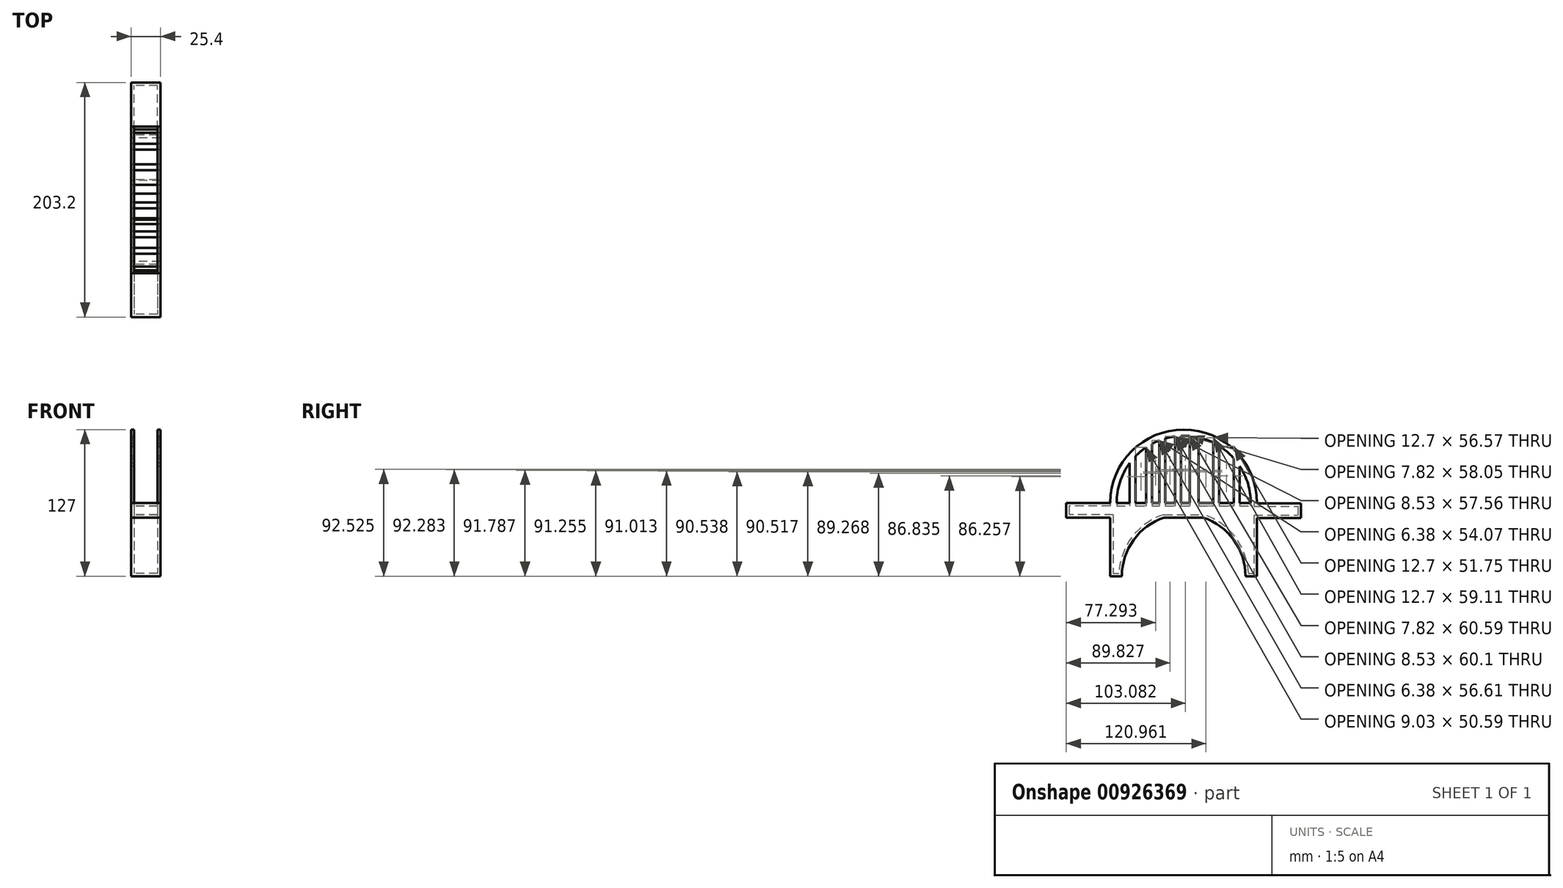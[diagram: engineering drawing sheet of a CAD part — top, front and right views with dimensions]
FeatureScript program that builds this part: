
annotation { "Feature Type Name" : "Feature", "Feature Type Description" : "" }
export const myFeature = defineFeature(function(context is Context, id is Id, definition is map)
    precondition{}
    {
        {
            var Q0;
            Q0=qCreatedBy(makeId("Right.planeOp"),FACE);
            var sketch = newSketch(context, id + "F0", { "sketchPlane" : qUnion([Q0])});
            skLineSegment(sketch, "E0.bottom", {"start": v(-51.78, 37.28) * mm, "end": v(75.22, 37.28) * mm});
            skLineSegment(sketch, "E0.top", {"start": v(-51.78, 24.58) * mm, "end": v(75.22, 24.58) * mm});
            skLineSegment(sketch, "E0.left", {"start": v(-51.78, 37.28) * mm, "end": v(-51.78, 24.58) * mm});
            skLineSegment(sketch, "E0.right", {"start": v(75.22, 37.28) * mm, "end": v(75.22, 24.58) * mm});
            skLineSegment(sketch, "E1.top", {"start": v(-51.78, -26.22) * mm, "end": v(75.22, -26.22) * mm});
            skLineSegment(sketch, "E1.left", {"start": v(-51.78, 24.58) * mm, "end": v(-51.78, -26.22) * mm});
            skLineSegment(sketch, "E1.right", {"start": v(75.22, 24.58) * mm, "end": v(75.22, -26.22) * mm});
            skArc(sketch, "E2", {"start": v(-41.8, -26.22) * mm, "mid": v(11.72, 27.3) * mm, "end": v(65.23, -26.22) * mm});
            skLineSegment(sketch, "E3.bottom", {"start": v(75.22, 36.8) * mm, "end": v(113.32, 36.8) * mm});
            skLineSegment(sketch, "E3.top", {"start": v(75.22, 24.1) * mm, "end": v(113.32, 24.1) * mm});
            skLineSegment(sketch, "E3.left", {"start": v(75.22, 36.8) * mm, "end": v(75.22, 24.1) * mm});
            skLineSegment(sketch, "E3.right", {"start": v(113.32, 36.8) * mm, "end": v(113.32, 24.1) * mm});
            skLineSegment(sketch, "E4.bottom", {"start": v(-51.78, 37.28) * mm, "end": v(-89.88, 37.28) * mm});
            skLineSegment(sketch, "E4.top", {"start": v(-51.78, 24.58) * mm, "end": v(-89.88, 24.58) * mm});
            skLineSegment(sketch, "E4.right", {"start": v(-89.88, 37.28) * mm, "end": v(-89.88, 24.58) * mm});
            skArc(sketch, "E5", {"start": v(75.22, 37.28) * mm, "mid": v(11.72, 100.78) * mm, "end": v(-51.78, 37.28) * mm});
            skArc(sketch, "E6", {"start": v(69.76, 37.28) * mm, "mid": v(11.72, 95.33) * mm, "end": v(-46.33, 37.28) * mm});
            skLineSegment(sketch, "E7", {"start": v(-34.97, 71.79) * mm, "end": v(-34.97, 37.28) * mm});
            skLineSegment(sketch, "E8", {"start": v(-29.89, 77.77) * mm, "end": v(-29.89, 37.28) * mm});
            skLineSegment(sketch, "E9", {"start": v(-20.85, 85.33) * mm, "end": v(-20.85, 37.28) * mm});
            skLineSegment(sketch, "E10", {"start": v(-15.77, 88.4) * mm, "end": v(-15.77, 37.28) * mm});
            skLineSegment(sketch, "E11", {"start": v(-9.4, 91.35) * mm, "end": v(-9.4, 37.28) * mm});
            skLineSegment(sketch, "E12", {"start": v(-4.32, 93.07) * mm, "end": v(-4.32, 37.28) * mm});
            skLineSegment(sketch, "E13", {"start": v(17.11, 95.08) * mm, "end": v(17.11, 37.28) * mm});
            skLineSegment(sketch, "E14", {"start": v(24.73, 93.85) * mm, "end": v(24.73, 37.28) * mm});
            skLineSegment(sketch, "E15", {"start": v(37.43, 89.32) * mm, "end": v(37.43, 37.28) * mm});
            skLineSegment(sketch, "E16", {"start": v(42.51, 86.49) * mm, "end": v(42.51, 37.28) * mm});
            skLineSegment(sketch, "E17", {"start": v(55.21, 75.72) * mm, "end": v(55.21, 37.28) * mm});
            skLineSegment(sketch, "E18", {"start": v(60.3, 69.06) * mm, "end": v(60.3, 37.28) * mm});
            skLineSegment(sketch, "E19", {"start": v(4.21, 94.84) * mm, "end": v(4.21, 37.28) * mm});
            skLineSegment(sketch, "E20", {"start": v(9.3, 95.28) * mm, "end": v(9.3, 37.28) * mm});
            skPoint(sketch, "E21.startSnap0", {"position": v(55.21, 56.5) * mm});
            skSolve(sketch);
        }
        {
            var Q0;
            {var subQ0=sQuery(id+"F0.wireOp",EDGE,"E1.left");Q0=makeQuery(id+"F0.imprint","IMPRINT",FACE,{"disambiguationData":[TD([[makeQuery(id+"F0.imprint","IMPRINT",EDGE,{"derivedFrom":subQ0}),1.0]])]});}
            var Q1;
            {var subQ2=sQuery(id+"F0.wireOp",EDGE,"E1.top");var subQ4=sQuery(id+"F0.wireOp",EDGE,"E2");var subQ5=makeQuery(id+"F0.imprint","INTERSECT",VERTEX,{"disambiguationData":[OD(1.0)],"derivedFrom":[subQ2,subQ4]});Q1=makeQuery(id+"F0.imprint","IMPRINT",FACE,{"disambiguationData":[TD([[makeQuery(id+"F0.imprint","IMPRINT",EDGE,{"disambiguationData":[TD([[subQ5,-1.0]])],"derivedFrom":subQ2}),1.0]])]});}
            var Q2;
            {var subQ7=sQuery(id+"F0.wireOp",EDGE,"E0.left");Q2=makeQuery(id+"F0.imprint","IMPRINT",FACE,{"disambiguationData":[TD([[makeQuery(id+"F0.imprint","IMPRINT",EDGE,{"derivedFrom":subQ7}),1.0]])]});}
            var Q3;
            Q3=makeQuery(id+"F0.imprint","IMPRINT",FACE,{"disambiguationData":[TD([[makeQuery(id+"F0.imprint","IMPRINT",EDGE,{"derivedFrom":sQuery(id+"F0.wireOp",EDGE,"E0.left")}),-1.0]])]});
            var Q4;
            {var subQ0=sQuery(id+"F0.wireOp",EDGE,"E3.bottom");Q4=makeQuery(id+"F0.imprint","IMPRINT",FACE,{"disambiguationData":[TD([[makeQuery(id+"F0.imprint","IMPRINT",EDGE,{"derivedFrom":subQ0}),-1.0]])]});}
            var Q5;
            {var subQ0=sQuery(id+"F0.wireOp",EDGE,"E2");var subQ1=sQuery(id+"F0.wireOp",EDGE,"E0.top");var subQ2=makeQuery(id+"F0.imprint","INTERSECT",VERTEX,{"disambiguationData":[OD(0.0)],"derivedFrom":[subQ1,subQ0]});Q5=makeQuery(id+"F0.imprint","IMPRINT",FACE,{"disambiguationData":[TD([[makeQuery(id+"F0.imprint","IMPRINT",EDGE,{"disambiguationData":[TD([[subQ2,1.0]])],"derivedFrom":subQ1}),1.0]])]});}
            var Q6;
            {var subQ8=sQuery(id+"F0.wireOp",EDGE,"E5");Q6=makeQuery(id+"F0.imprint","IMPRINT",FACE,{"disambiguationData":[TD([[makeQuery(id+"F0.imprint","IMPRINT",EDGE,{"derivedFrom":subQ8}),1.0]])]});}
            var Q7;
            {var subQ0=sQuery(id+"F0.wireOp",EDGE,"E7");Q7=makeQuery(id+"F0.imprint","IMPRINT",FACE,{"disambiguationData":[TD([[makeQuery(id+"F0.imprint","IMPRINT",EDGE,{"derivedFrom":subQ0}),1.0]])]});}
            var Q8;
            {var subQ0=sQuery(id+"F0.wireOp",EDGE,"E9");Q8=makeQuery(id+"F0.imprint","IMPRINT",FACE,{"disambiguationData":[TD([[makeQuery(id+"F0.imprint","IMPRINT",EDGE,{"derivedFrom":subQ0}),1.0]])]});}
            var Q9;
            {var subQ0=sQuery(id+"F0.wireOp",EDGE,"E11");Q9=makeQuery(id+"F0.imprint","IMPRINT",FACE,{"disambiguationData":[TD([[makeQuery(id+"F0.imprint","IMPRINT",EDGE,{"derivedFrom":subQ0}),1.0]])]});}
            var Q10;
            {var subQ2=sQuery(id+"F0.wireOp",EDGE,"E19");Q10=makeQuery(id+"F0.imprint","IMPRINT",FACE,{"disambiguationData":[TD([[makeQuery(id+"F0.imprint","IMPRINT",EDGE,{"derivedFrom":subQ2}),1.0]])]});}
            var Q11;
            {var subQ0=sQuery(id+"F0.wireOp",EDGE,"E13");Q11=makeQuery(id+"F0.imprint","IMPRINT",FACE,{"disambiguationData":[TD([[makeQuery(id+"F0.imprint","IMPRINT",EDGE,{"derivedFrom":subQ0}),1.0]])]});}
            var Q12;
            {var subQ2=sQuery(id+"F0.wireOp",EDGE,"E15");Q12=makeQuery(id+"F0.imprint","IMPRINT",FACE,{"disambiguationData":[TD([[makeQuery(id+"F0.imprint","IMPRINT",EDGE,{"derivedFrom":subQ2}),1.0]])]});}
            var Q13;
            {var subQ0=sQuery(id+"F0.wireOp",EDGE,"E17");Q13=makeQuery(id+"F0.imprint","IMPRINT",FACE,{"disambiguationData":[TD([[makeQuery(id+"F0.imprint","IMPRINT",EDGE,{"derivedFrom":subQ0}),1.0]])]});}
            extrude(context, id + "F1", {"entities" : qUnion([Q0, Q1, Q2, Q3, Q4, Q5, Q6, Q7, Q8, Q9, Q10, Q11, Q12, Q13]), "depth" : 25.4 * mm, "offsetDistance" : 25.4 * mm});
        }
        {
            var Q0;
            {var subQ0=sQuery(id+"F0.wireOp",EDGE,"E6");Q0=makeQuery(id+"F1.opExtrude","SWEPT_FACE",FACE,{"disambiguationData":[OSD([subQ0]),TDD([makeQuery(id+"F0.imprint","IMPRINT",EDGE,{"disambiguationData":[TD([[makeQuery(id+"F0.imprint","INTERSECT",VERTEX,{"derivedFrom":[subQ0,sQuery(id+"F0.wireOp",EDGE,"E10")]}),1.0]])],"derivedFrom":subQ0})])]});}
            var Q1;
            {var subQ0=sQuery(id+"F0.wireOp",EDGE,"E6");Q1=makeQuery(id+"F1.opExtrude","SWEPT_FACE",FACE,{"disambiguationData":[OSD([subQ0]),TDD([makeQuery(id+"F0.imprint","IMPRINT",EDGE,{"disambiguationData":[TD([[makeQuery(id+"F0.imprint","INTERSECT",VERTEX,{"derivedFrom":[subQ0,sQuery(id+"F0.wireOp",EDGE,"E8")]}),1.0]])],"derivedFrom":subQ0})])]});}
            var Q2;
            {var subQ0=sQuery(id+"F0.wireOp",EDGE,"E6");Q2=makeQuery(id+"F1.opExtrude","SWEPT_FACE",FACE,{"disambiguationData":[OSD([subQ0]),TDD([makeQuery(id+"F0.imprint","IMPRINT",EDGE,{"disambiguationData":[TD([[makeQuery(id+"F0.imprint","INTERSECT",VERTEX,{"disambiguationData":[OD(1.0)],"derivedFrom":[sQuery(id+"F0.wireOp",EDGE,"E0.bottom"),subQ0]}),1.0]])],"derivedFrom":subQ0})])]});}
            var Q3;
            {var subQ0=sQuery(id+"F0.wireOp",EDGE,"E6");Q3=makeQuery(id+"F1.opExtrude","SWEPT_FACE",FACE,{"disambiguationData":[OSD([subQ0]),TDD([makeQuery(id+"F0.imprint","IMPRINT",EDGE,{"disambiguationData":[TD([[makeQuery(id+"F0.imprint","INTERSECT",VERTEX,{"derivedFrom":[subQ0,sQuery(id+"F0.wireOp",EDGE,"E12")]}),1.0]])],"derivedFrom":subQ0})])]});}
            var Q4;
            {var subQ0=sQuery(id+"F0.wireOp",EDGE,"E6");Q4=makeQuery(id+"F1.opExtrude","SWEPT_FACE",FACE,{"disambiguationData":[OSD([subQ0]),TDD([makeQuery(id+"F0.imprint","IMPRINT",EDGE,{"disambiguationData":[TD([[makeQuery(id+"F0.imprint","INTERSECT",VERTEX,{"derivedFrom":[subQ0,sQuery(id+"F0.wireOp",EDGE,"E13")]}),-1.0]])],"derivedFrom":subQ0})])]});}
            var Q5;
            {var subQ0=sQuery(id+"F0.wireOp",EDGE,"E6");Q5=makeQuery(id+"F1.opExtrude","SWEPT_FACE",FACE,{"disambiguationData":[OSD([subQ0]),TDD([makeQuery(id+"F0.imprint","IMPRINT",EDGE,{"disambiguationData":[TD([[makeQuery(id+"F0.imprint","INTERSECT",VERTEX,{"derivedFrom":[subQ0,sQuery(id+"F0.wireOp",EDGE,"E14")]}),1.0]])],"derivedFrom":subQ0})])]});}
            var Q6;
            {var subQ0=sQuery(id+"F0.wireOp",EDGE,"E6");Q6=makeQuery(id+"F1.opExtrude","SWEPT_FACE",FACE,{"disambiguationData":[OSD([subQ0]),TDD([makeQuery(id+"F0.imprint","IMPRINT",EDGE,{"disambiguationData":[TD([[makeQuery(id+"F0.imprint","INTERSECT",VERTEX,{"derivedFrom":[subQ0,sQuery(id+"F0.wireOp",EDGE,"E16")]}),1.0]])],"derivedFrom":subQ0})])]});}
            var Q7;
            {var subQ0=sQuery(id+"F0.wireOp",EDGE,"E6");Q7=makeQuery(id+"F1.opExtrude","SWEPT_FACE",FACE,{"disambiguationData":[OSD([subQ0]),TDD([makeQuery(id+"F0.imprint","IMPRINT",EDGE,{"disambiguationData":[TD([[makeQuery(id+"F0.imprint","INTERSECT",VERTEX,{"disambiguationData":[OD(0.0)],"derivedFrom":[sQuery(id+"F0.wireOp",EDGE,"E0.bottom"),subQ0]}),-1.0]])],"derivedFrom":subQ0})])]});}
            var Q8;
            Q8=makeQuery(id+"F1.opExtrude","SWEPT_FACE",FACE,{"disambiguationData":[OSD([sQuery(id+"F0.wireOp",EDGE,"E5")])]});
            var Q9;
            Q9=makeQuery(id+"F1.opExtrude","SWEPT_FACE",FACE,{"disambiguationData":[OSD([sQuery(id+"F0.wireOp",EDGE,"E7")])]});
            var Q10;
            Q10=makeQuery(id+"F1.opExtrude","SWEPT_FACE",FACE,{"disambiguationData":[OSD([sQuery(id+"F0.wireOp",EDGE,"E8")])]});
            var Q11;
            Q11=makeQuery(id+"F1.opExtrude","SWEPT_FACE",FACE,{"disambiguationData":[OSD([sQuery(id+"F0.wireOp",EDGE,"E10")])]});
            var Q12;
            Q12=makeQuery(id+"F1.opExtrude","SWEPT_FACE",FACE,{"disambiguationData":[OSD([sQuery(id+"F0.wireOp",EDGE,"E12")])]});
            var Q13;
            Q13=makeQuery(id+"F1.opExtrude","SWEPT_FACE",FACE,{"disambiguationData":[OSD([sQuery(id+"F0.wireOp",EDGE,"E20")])]});
            var Q14;
            Q14=makeQuery(id+"F1.opExtrude","SWEPT_FACE",FACE,{"disambiguationData":[OSD([sQuery(id+"F0.wireOp",EDGE,"E14")])]});
            var Q15;
            Q15=makeQuery(id+"F1.opExtrude","SWEPT_FACE",FACE,{"disambiguationData":[OSD([sQuery(id+"F0.wireOp",EDGE,"E16")])]});
            var Q16;
            Q16=makeQuery(id+"F1.opExtrude","SWEPT_FACE",FACE,{"disambiguationData":[OSD([sQuery(id+"F0.wireOp",EDGE,"E18")])]});
            var Q17;
            Q17=makeQuery(id+"F1.opExtrude","SWEPT_FACE",FACE,{"disambiguationData":[OSD([sQuery(id+"F0.wireOp",EDGE,"E9")])]});
            var Q18;
            Q18=makeQuery(id+"F1.opExtrude","SWEPT_FACE",FACE,{"disambiguationData":[OSD([sQuery(id+"F0.wireOp",EDGE,"E11")])]});
            var Q19;
            Q19=makeQuery(id+"F1.opExtrude","SWEPT_FACE",FACE,{"disambiguationData":[OSD([sQuery(id+"F0.wireOp",EDGE,"E19")])]});
            var Q20;
            Q20=makeQuery(id+"F1.opExtrude","SWEPT_FACE",FACE,{"disambiguationData":[OSD([sQuery(id+"F0.wireOp",EDGE,"E13")])]});
            var Q21;
            Q21=makeQuery(id+"F1.opExtrude","SWEPT_FACE",FACE,{"disambiguationData":[OSD([sQuery(id+"F0.wireOp",EDGE,"E15")])]});
            var Q22;
            Q22=makeQuery(id+"F1.opExtrude","SWEPT_FACE",FACE,{"disambiguationData":[OSD([sQuery(id+"F0.wireOp",EDGE,"E17")])]});
            shell(context, id + "F2", {"entities" : qUnion([Q0, Q1, Q2, Q3, Q4, Q5, Q6, Q7, Q8, Q9, Q10, Q11, Q12, Q13, Q14, Q15, Q16, Q17, Q18, Q19, Q20, Q21, Q22]), "thickness" : 2.54 * mm});
        }
    });
